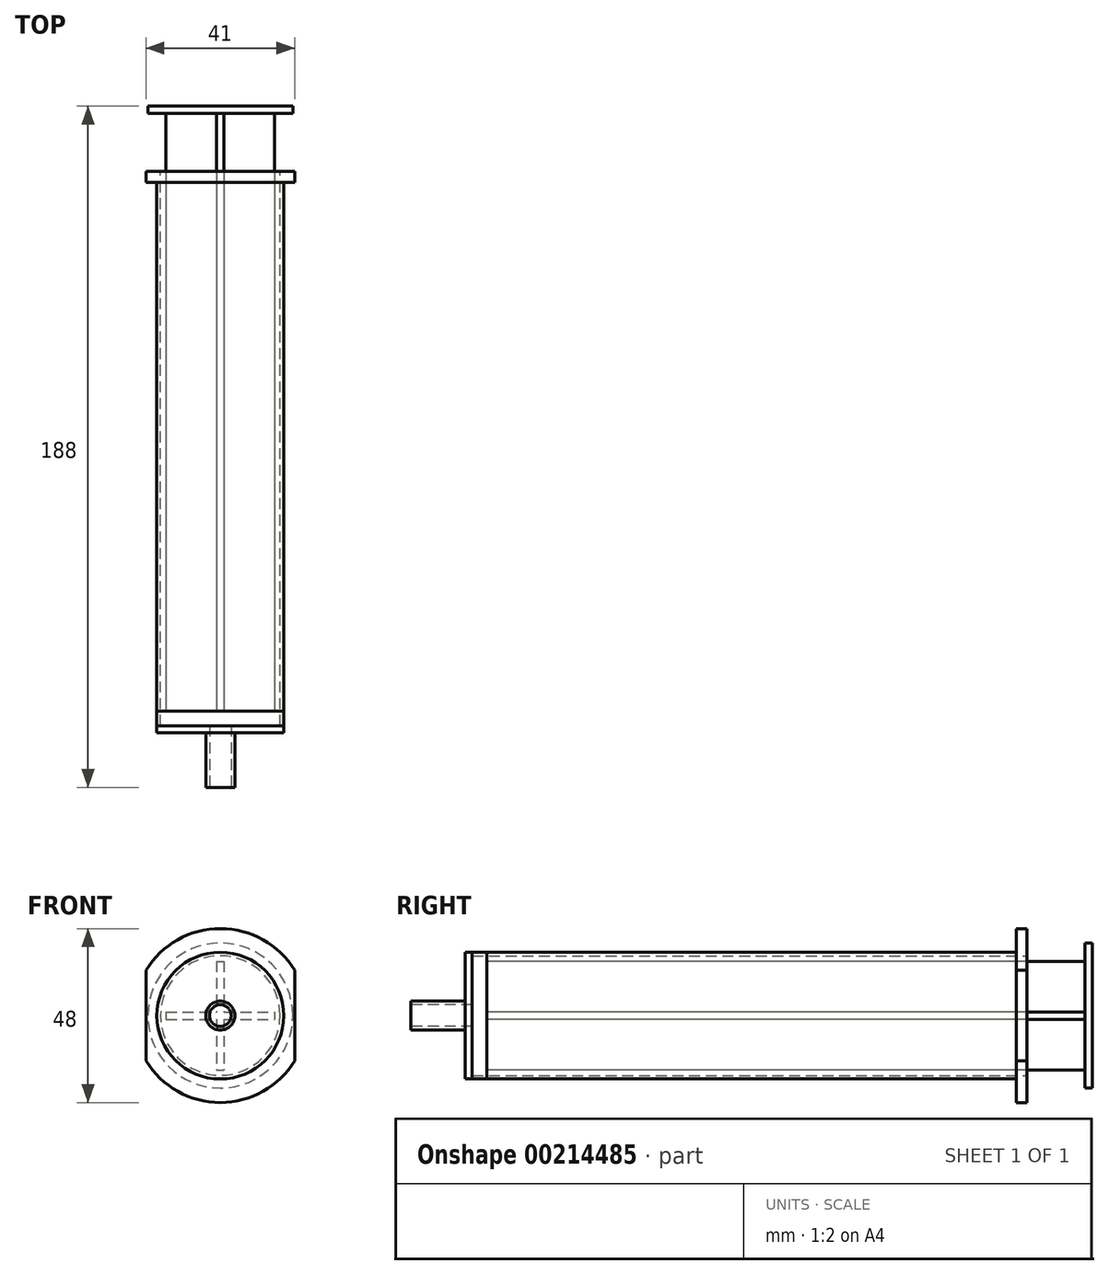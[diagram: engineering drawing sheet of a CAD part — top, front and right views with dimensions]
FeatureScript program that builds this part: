
annotation { "Feature Type Name" : "Feature", "Feature Type Description" : "" }
export const myFeature = defineFeature(function(context is Context, id is Id, definition is map)
    precondition{}
    {
        {
            var Q0;
            Q0=qCreatedBy(makeId("Front.planeOp"),FACE);
            var sketch = newSketch(context, id + "F0", { "sketchPlane" : qUnion([Q0])});
            skCircle(sketch, "E0", {"center": v(0, 0) * mm, "radius": 16.5 * mm});
            skCircle(sketch, "E1", {"center": v(0, 0) * mm, "radius": 17.5 * mm});
            skSolve(sketch);
        }
        {
            var Q0;
            Q0=qSketchRegion(id+"F0",true);
            extrude(context, id + "F1", {"entities" : qUnion([Q0]), "depth" : 150 * mm});
        }
        {
            var Q0;
            Q0=makeQuery(id+"F1.opExtrude","CAP_FACE",FACE,{"disambiguationData":[OSD([sQuery(id+"F0.wireOp",EDGE,"E0"),sQuery(id+"F0.wireOp",EDGE,"E1")])],"isStart":false});
            var sketch = newSketch(context, id + "F2", { "sketchPlane" : qUnion([Q0])});
            skCircle(sketch, "E2", {"center": v(0, 0) * mm, "radius": 17.5 * mm});
            skSolve(sketch);
        }
        {
            var Q0;
            Q0=qSketchRegion(id+"F2",true);
            extrude(context, id + "F3", {"entities" : qUnion([Q0]), "operationType" : NewBodyOperationType.ADD, "depth" : 2 * mm});
        }
        {
            var Q0;
            Q0=makeQuery(id+"F3.opExtrude","CAP_FACE",FACE,{"disambiguationData":[OSD([sQuery(id+"F2.wireOp",EDGE,"E2")])],"isStart":false});
            var sketch = newSketch(context, id + "F4", { "sketchPlane" : qUnion([Q0])});
            skCircle(sketch, "E3", {"center": v(0, 0) * mm, "radius": 4 * mm});
            skSolve(sketch);
        }
        {
            var Q0;
            Q0=qSketchRegion(id+"F4",true);
            extrude(context, id + "F5", {"entities" : qUnion([Q0]), "operationType" : NewBodyOperationType.ADD, "depth" : 15 * mm});
        }
        {
            var Q0;
            Q0=makeQuery(id+"F5.opExtrude","CAP_FACE",FACE,{"disambiguationData":[OSD([sQuery(id+"F4.wireOp",EDGE,"E3")])],"isStart":false});
            var sketch = newSketch(context, id + "F6", { "sketchPlane" : qUnion([Q0])});
            skCircle(sketch, "E4", {"center": v(0, 0) * mm, "radius": 3 * mm});
            skSolve(sketch);
        }
        {
            var Q0;
            Q0=qSketchRegion(id+"F6",true);
            var Q1;
            Q1=makeQuery(id+"F3.opExtrude","CAP_FACE",FACE,{"disambiguationData":[OSD([sQuery(id+"F2.wireOp",EDGE,"E2")])],"isStart":true});
            extrude(context, id + "F7", {"entities" : qUnion([Q0]), "operationType" : NewBodyOperationType.REMOVE, "endBound" : BoundingType.UP_TO_SURFACE, "oppositeDirection" : true, "endBoundEntityFace" : qUnion([Q1]), "depth" : 25 * mm});
        }
        {
            var Q0;
            Q0=makeQuery(id+"F1.opExtrude","CAP_FACE",FACE,{"disambiguationData":[OSD([sQuery(id+"F0.wireOp",EDGE,"E0"),sQuery(id+"F0.wireOp",EDGE,"E1")])],"isStart":true});
            var sketch = newSketch(context, id + "F8", { "sketchPlane" : qUnion([Q0])});
            skCircle(sketch, "E5", {"center": v(0, 0) * mm, "radius": 24 * mm});
            skLineSegment(sketch, "E6", {"start": v(-20.5, 12.48) * mm, "end": v(-20.5, -12.48) * mm});
            skLineSegment(sketch, "E7", {"start": v(20.5, 12.48) * mm, "end": v(20.5, -12.48) * mm});
            skSolve(sketch);
        }
        {
            var Q0;
            {var subQ1=sQuery(id+"F8.wireOp",EDGE,"E6");Q0=makeQuery(id+"F8.imprint","IMPRINT",FACE,{"disambiguationData":[TD([[makeQuery(id+"F8.imprint","IMPRINT",EDGE,{"derivedFrom":subQ1}),1.0]])]});}
            var Q1;
            Q1=makeQuery(id+"F8.imprint","IMPRINT",FACE,{"disambiguationData":[TD([[makeQuery(id+"F8.imprint","IMPRINT",EDGE,{"derivedFrom":makeQuery(id+"F1.opExtrude","CAP_EDGE",EDGE,{"disambiguationData":[OSD([sQuery(id+"F0.wireOp",EDGE,"E0")])],"isStart":true})}),1.0]])]});
            extrude(context, id + "F9", {"entities" : qUnion([Q0, Q1]), "operationType" : NewBodyOperationType.ADD, "depth" : 3 * mm});
        }
        {
            var Q0;
            Q0=makeQuery(id+"F3.opExtrude","CAP_FACE",FACE,{"disambiguationData":[OSD([sQuery(id+"F2.wireOp",EDGE,"E2")])],"isStart":true});
            var sketch = newSketch(context, id + "F10", { "sketchPlane" : qUnion([Q0])});
            skCircle(sketch, "E8", {"center": v(0, 0) * mm, "radius": 17.5 * mm});
            skSolve(sketch);
        }
        {
            var Q0;
            Q0=qSketchRegion(id+"F10",true);
            extrude(context, id + "F11", {"entities" : qUnion([Q0]), "depth" : 4 * mm});
        }
        {
            var Q0;
            Q0=makeQuery(id+"F11.opExtrude","CAP_FACE",FACE,{"disambiguationData":[OSD([sQuery(id+"F10.wireOp",EDGE,"E8")])],"isStart":false});
            var sketch = newSketch(context, id + "F12", { "sketchPlane" : qUnion([Q0])});
            skLineSegment(sketch, "E9.bottom", {"start": v(15, 1) * mm, "end": v(-15, 1) * mm});
            skLineSegment(sketch, "E9.top", {"start": v(15, -1) * mm, "end": v(-15, -1) * mm});
            skLineSegment(sketch, "E9.left", {"start": v(15, 1) * mm, "end": v(15, -1) * mm});
            skLineSegment(sketch, "E9.right", {"start": v(-15, 1) * mm, "end": v(-15, -1) * mm});
            skLineSegment(sketch, "E10.bottom", {"start": v(1, 15) * mm, "end": v(-1, 15) * mm});
            skLineSegment(sketch, "E10.top", {"start": v(1, -15) * mm, "end": v(-1, -15) * mm});
            skLineSegment(sketch, "E10.left", {"start": v(1, 15) * mm, "end": v(1, -15) * mm});
            skLineSegment(sketch, "E10.right", {"start": v(-1, 15) * mm, "end": v(-1, -15) * mm});
            skSolve(sketch);
        }
        {
            var Q0;
            Q0=qSketchRegion(id+"F12",true);
            extrude(context, id + "F13", {"entities" : qUnion([Q0]), "operationType" : NewBodyOperationType.ADD, "depth" : 165 * mm});
        }
        {
            var Q0;
            Q0=makeQuery(id+"F13.opExtrude","CAP_FACE",FACE,{"disambiguationData":[OSD([sQuery(id+"F12.wireOp",EDGE,"E9.bottom"),sQuery(id+"F12.wireOp",EDGE,"E9.top"),sQuery(id+"F12.wireOp",EDGE,"E9.left"),sQuery(id+"F12.wireOp",EDGE,"E9.right"),sQuery(id+"F12.wireOp",EDGE,"E10.bottom"),sQuery(id+"F12.wireOp",EDGE,"E10.top"),sQuery(id+"F12.wireOp",EDGE,"E10.left"),sQuery(id+"F12.wireOp",EDGE,"E10.right")])],"isStart":false});
            var sketch = newSketch(context, id + "F14", { "sketchPlane" : qUnion([Q0])});
            skCircle(sketch, "E11", {"center": v(0, 0) * mm, "radius": 20 * mm});
            skSolve(sketch);
        }
        {
            var Q0;
            Q0=qSketchRegion(id+"F14",true);
            extrude(context, id + "F15", {"entities" : qUnion([Q0]), "operationType" : NewBodyOperationType.ADD, "depth" : 2 * mm});
        }
    });
